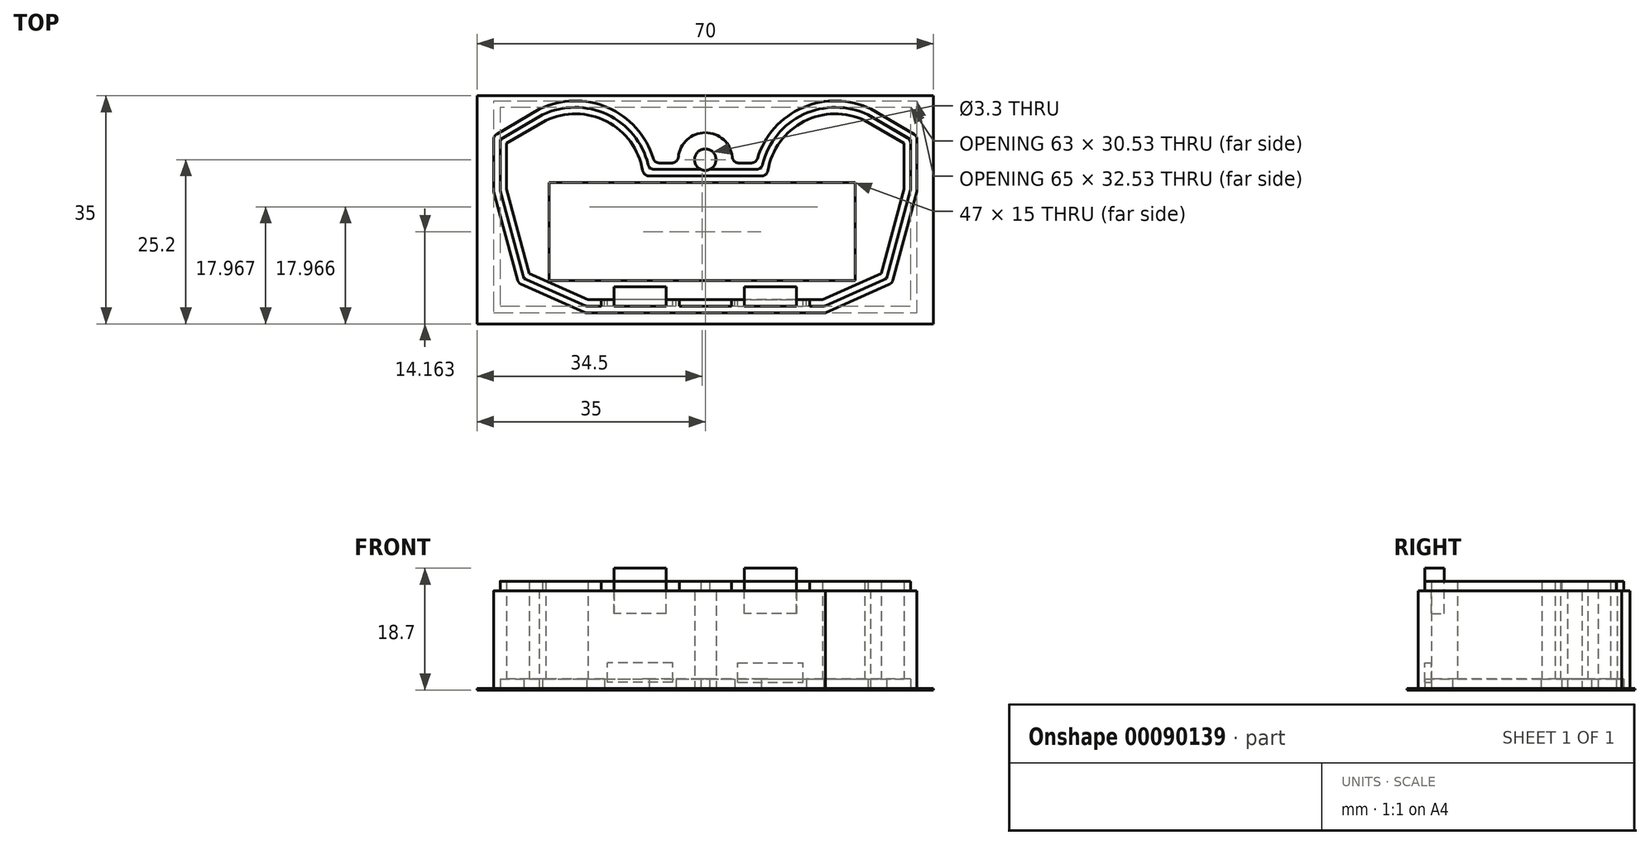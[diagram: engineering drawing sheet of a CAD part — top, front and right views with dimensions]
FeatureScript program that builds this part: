
annotation { "Feature Type Name" : "Feature", "Feature Type Description" : "" }
export const myFeature = defineFeature(function(context is Context, id is Id, definition is map)
    precondition{}
    {
        {
            var Q0;
            Q0=qCreatedBy(makeId("Top.planeOp"),FACE);
            var sketch = newSketch(context, id + "F0", { "sketchPlane" : qUnion([Q0])});
            skLineSegment(sketch, "E0", {"start": v(-31.6, 0) * mm, "end": v(0, 0) * mm, "construction": true});
            skLineSegment(sketch, "E1", {"start": v(-18, 0) * mm, "end": v(0, 0) * mm});
            skLineSegment(sketch, "E2", {"start": v(-27, 4) * mm, "end": v(0, 4) * mm, "construction": true});
            skLineSegment(sketch, "E3", {"start": v(-18, 0) * mm, "end": v(-27, 4) * mm});
            skLineSegment(sketch, "E4", {"start": v(-30.5, 17) * mm, "end": v(0, 17) * mm, "construction": true});
            skLineSegment(sketch, "E5", {"start": v(-30.5, 17) * mm, "end": v(-30.5, 24) * mm});
            skLineSegment(sketch, "E6", {"start": v(-30.5, 17) * mm, "end": v(-27, 4) * mm});
            skArc(sketch, "E7", {"start": v(0, 23.15) * mm, "mid": v(-1.65, 21.5) * mm, "end": v(0, 19.85) * mm});
            skLineSegment(sketch, "E8", {"start": v(0, 0) * mm, "end": v(0, 42.85) * mm, "construction": true});
            skLineSegment(sketch, "E9", {"start": v(-30.5, 24) * mm, "end": v(-24.5, 27.5) * mm});
            skLineSegment(sketch, "E10", {"start": v(0, 19) * mm, "end": v(-9.5, 19) * mm});
            skArc(sketch, "E11", {"start": v(-9.5, 19) * mm, "mid": v(-14.78, 27.17) * mm, "end": v(-24.5, 27.5) * mm});
            skLineSegment(sketch, "E12.0", {"start": v(-18.21, -1) * mm, "end": v(0, -1) * mm});
            skLineSegment(sketch, "E12.1", {"start": v(-18.21, -1) * mm, "end": v(-27.84, 3.28) * mm});
            skLineSegment(sketch, "E12.2", {"start": v(-31.5, 16.87) * mm, "end": v(-27.84, 3.28) * mm});
            skLineSegment(sketch, "E12.3", {"start": v(-0.69, 20) * mm, "end": v(-8.62, 20) * mm});
            skArc(sketch, "E12.4", {"start": v(-8.62, 20) * mm, "mid": v(-14.7, 28.27) * mm, "end": v(-24.97, 28.38) * mm});
            skLineSegment(sketch, "E12.5", {"start": v(-31.5, 24.57) * mm, "end": v(-24.97, 28.38) * mm});
            skLineSegment(sketch, "E12.6", {"start": v(-31.5, 16.87) * mm, "end": v(-31.5, 24.57) * mm});
            skLineSegment(sketch, "E13.MirrorCS", {"start": v(30.5, 24) * mm, "end": v(24.5, 27.5) * mm});
            skLineSegment(sketch, "E14.MirrorCS", {"start": v(18, 0) * mm, "end": v(0, 0) * mm});
            skLineSegment(sketch, "E15.MirrorCS", {"start": v(31.5, 16.87) * mm, "end": v(27.84, 3.28) * mm});
            skArc(sketch, "E16.MirrorCS", {"start": v(0, 23.15) * mm, "mid": v(1.65, 21.5) * mm, "end": v(0, 19.85) * mm});
            skLineSegment(sketch, "E17.MirrorCS", {"start": v(18, 0) * mm, "end": v(27, 4) * mm});
            skLineSegment(sketch, "E18.MirrorCS", {"start": v(30.5, 17) * mm, "end": v(27, 4) * mm});
            skLineSegment(sketch, "E19.MirrorCS", {"start": v(31.5, 24.57) * mm, "end": v(24.97, 28.38) * mm});
            skLineSegment(sketch, "E20.MirrorCS", {"start": v(27, 4) * mm, "end": v(0, 4) * mm, "construction": true});
            skArc(sketch, "E21.MirrorCS", {"start": v(9.5, 19) * mm, "mid": v(14.78, 27.17) * mm, "end": v(24.5, 27.5) * mm});
            skLineSegment(sketch, "E22.MirrorCS", {"start": v(31.5, 16.87) * mm, "end": v(31.5, 24.57) * mm});
            skLineSegment(sketch, "E23.MirrorCS", {"start": v(31.6, 0) * mm, "end": v(0, 0) * mm, "construction": true});
            skLineSegment(sketch, "E24.MirrorCS", {"start": v(18.21, -1) * mm, "end": v(0, -1) * mm});
            skLineSegment(sketch, "E25.MirrorCS", {"start": v(0.69, 20) * mm, "end": v(8.62, 20) * mm});
            skLineSegment(sketch, "E26.MirrorCS", {"start": v(18.21, -1) * mm, "end": v(27.84, 3.28) * mm});
            skLineSegment(sketch, "E27.MirrorCS", {"start": v(0, 19) * mm, "end": v(9.5, 19) * mm});
            skLineSegment(sketch, "E28.MirrorCS", {"start": v(30.5, 17) * mm, "end": v(30.5, 24) * mm});
            skArc(sketch, "E29.MirrorCS", {"start": v(8.62, 20) * mm, "mid": v(14.7, 28.27) * mm, "end": v(24.97, 28.38) * mm});
            skLineSegment(sketch, "E30.0", {"start": v(-18.42, -2) * mm, "end": v(0, -2) * mm});
            skLineSegment(sketch, "E30.1", {"start": v(18.42, -2) * mm, "end": v(0, -2) * mm});
            skLineSegment(sketch, "E30.2", {"start": v(18.42, -2) * mm, "end": v(28.68, 2.56) * mm});
            skArc(sketch, "E30.3", {"start": v(-7.81, 21) * mm, "mid": v(-14.65, 29.35) * mm, "end": v(-25.44, 29.27) * mm});
            skLineSegment(sketch, "E30.4", {"start": v(-32.5, 25.15) * mm, "end": v(-25.44, 29.27) * mm});
            skLineSegment(sketch, "E30.5", {"start": v(-32.5, 16.74) * mm, "end": v(-32.5, 25.15) * mm});
            skLineSegment(sketch, "E30.6", {"start": v(-32.5, 16.74) * mm, "end": v(-28.68, 2.56) * mm});
            skLineSegment(sketch, "E30.7", {"start": v(-4.12, 21) * mm, "end": v(-7.81, 21) * mm});
            skLineSegment(sketch, "E30.8", {"start": v(4.12, 21) * mm, "end": v(7.81, 21) * mm});
            skArc(sketch, "E30.9", {"start": v(7.81, 21) * mm, "mid": v(14.65, 29.35) * mm, "end": v(25.44, 29.27) * mm});
            skLineSegment(sketch, "E30.10", {"start": v(-18.42, -2) * mm, "end": v(-28.68, 2.56) * mm});
            skLineSegment(sketch, "E30.11", {"start": v(32.5, 25.15) * mm, "end": v(25.44, 29.27) * mm});
            skLineSegment(sketch, "E30.12", {"start": v(32.5, 16.74) * mm, "end": v(32.5, 25.15) * mm});
            skLineSegment(sketch, "E30.13", {"start": v(32.5, 16.74) * mm, "end": v(28.68, 2.56) * mm});
            skArc(sketch, "E31.0", {"start": v(0, 25.65) * mm, "mid": v(-3.1, 24.25) * mm, "end": v(-4.12, 21) * mm});
            skArc(sketch, "E31.1", {"start": v(0, 25.65) * mm, "mid": v(3.1, 24.25) * mm, "end": v(4.12, 21) * mm});
            skPoint(sketch, "E32.orphan", {"position": v(0, 20) * mm});
            skSolve(sketch);
        }
        {
            var Q0;
            Q0=makeQuery(id+"F0.imprint","IMPRINT",FACE,{"disambiguationData":[TD([[makeQuery(id+"F0.imprint","IMPRINT",EDGE,{"derivedFrom":sQuery(id+"F0.wireOp",EDGE,"E1")}),-1.0]])]});
            extrude(context, id + "F1", {"entities" : qUnion([Q0]), "depth" : 1.5 * mm, "offsetDistance" : 25 * mm});
        }
        {
            var Q0;
            Q0 = qSketchRegion(id + "F0", true);
            var Q1;
            Q1=makeQuery(id+"F1.opExtrude","CAP_FACE",FACE,{"disambiguationData":[OSD([sQuery(id+"F0.wireOp",EDGE,"E1"),sQuery(id+"F0.wireOp",EDGE,"E3"),sQuery(id+"F0.wireOp",EDGE,"E5"),sQuery(id+"F0.wireOp",EDGE,"E6"),sQuery(id+"F0.wireOp",EDGE,"E7"),sQuery(id+"F0.wireOp",EDGE,"E9"),sQuery(id+"F0.wireOp",EDGE,"E10"),sQuery(id+"F0.wireOp",EDGE,"E11"),sQuery(id+"F0.wireOp",EDGE,"E12.0"),sQuery(id+"F0.wireOp",EDGE,"E12.1"),sQuery(id+"F0.wireOp",EDGE,"E12.2"),sQuery(id+"F0.wireOp",EDGE,"E12.3"),sQuery(id+"F0.wireOp",EDGE,"E12.4"),sQuery(id+"F0.wireOp",EDGE,"E12.5"),sQuery(id+"F0.wireOp",EDGE,"E12.6"),sQuery(id+"F0.wireOp",EDGE,"E13.MirrorCS"),sQuery(id+"F0.wireOp",EDGE,"E14.MirrorCS"),sQuery(id+"F0.wireOp",EDGE,"E15.MirrorCS"),sQuery(id+"F0.wireOp",EDGE,"E16.MirrorCS"),sQuery(id+"F0.wireOp",EDGE,"E17.MirrorCS"),sQuery(id+"F0.wireOp",EDGE,"E18.MirrorCS"),sQuery(id+"F0.wireOp",EDGE,"E19.MirrorCS"),sQuery(id+"F0.wireOp",EDGE,"E21.MirrorCS"),sQuery(id+"F0.wireOp",EDGE,"E22.MirrorCS"),sQuery(id+"F0.wireOp",EDGE,"E24.MirrorCS"),sQuery(id+"F0.wireOp",EDGE,"E25.MirrorCS"),sQuery(id+"F0.wireOp",EDGE,"E26.MirrorCS"),sQuery(id+"F0.wireOp",EDGE,"E27.MirrorCS"),sQuery(id+"F0.wireOp",EDGE,"E28.MirrorCS"),sQuery(id+"F0.wireOp",EDGE,"E29.MirrorCS")])],"isStart":true});
            extrude(context, id + "F2", {"entities" : qUnion([Q0, Q1]), "operationType" : NewBodyOperationType.ADD, "surfaceOperationType" : NewSurfaceOperationType.ADD, "oppositeDirection" : true, "depth" : 15 * mm, "offsetDistance" : 25 * mm});
        }
        {
            var Q0;
            Q0=makeQuery(id+"F2.opExtrude","SWEPT_EDGE",EDGE,{"disambiguationData":[OSD([sQuery(id+"F0.wireOp",EDGE,"E30.8"),sQuery(id+"F0.wireOp",EDGE,"E30.9")])]});
            var Q1;
            Q1=makeQuery(id+"F2.opExtrude","SWEPT_EDGE",EDGE,{"disambiguationData":[OSD([sQuery(id+"F0.wireOp",EDGE,"E30.3"),sQuery(id+"F0.wireOp",EDGE,"E30.7")])]});
            var Q2;
            Q2=makeQuery(id+"F2.opExtrude","SWEPT_EDGE",EDGE,{"disambiguationData":[OSD([sQuery(id+"F0.wireOp",EDGE,"E30.7"),sQuery(id+"F0.wireOp",EDGE,"E31.0")])]});
            var Q3;
            Q3=makeQuery(id+"F2.opExtrude","SWEPT_EDGE",EDGE,{"disambiguationData":[OSD([sQuery(id+"F0.wireOp",EDGE,"E30.8"),sQuery(id+"F0.wireOp",EDGE,"E31.1")])]});
            var Q4;
            Q4=makeQuery(id+"F2.opExtrude","SWEPT_EDGE",EDGE,{"disambiguationData":[OSD([sQuery(id+"F0.wireOp",EDGE,"E30.11"),sQuery(id+"F0.wireOp",EDGE,"E30.12")])]});
            var Q5;
            Q5=makeQuery(id+"F2.opExtrude","SWEPT_EDGE",EDGE,{"disambiguationData":[OSD([sQuery(id+"F0.wireOp",EDGE,"E30.12"),sQuery(id+"F0.wireOp",EDGE,"E30.13")])]});
            var Q6;
            Q6=makeQuery(id+"F2.opExtrude","SWEPT_EDGE",EDGE,{"disambiguationData":[OSD([sQuery(id+"F0.wireOp",EDGE,"E30.2"),sQuery(id+"F0.wireOp",EDGE,"E30.13")])]});
            var Q7;
            Q7=makeQuery(id+"F2.opExtrude","SWEPT_EDGE",EDGE,{"disambiguationData":[OSD([sQuery(id+"F0.wireOp",EDGE,"E30.0"),sQuery(id+"F0.wireOp",EDGE,"E30.10")])]});
            var Q8;
            Q8=makeQuery(id+"F2.opExtrude","SWEPT_EDGE",EDGE,{"disambiguationData":[OSD([sQuery(id+"F0.wireOp",EDGE,"E30.6"),sQuery(id+"F0.wireOp",EDGE,"E30.10")])]});
            var Q9;
            Q9=makeQuery(id+"F2.opExtrude","SWEPT_EDGE",EDGE,{"disambiguationData":[OSD([sQuery(id+"F0.wireOp",EDGE,"E30.5"),sQuery(id+"F0.wireOp",EDGE,"E30.6")])]});
            var Q10;
            Q10=makeQuery(id+"F2.opExtrude","SWEPT_EDGE",EDGE,{"disambiguationData":[OSD([sQuery(id+"F0.wireOp",EDGE,"E30.4"),sQuery(id+"F0.wireOp",EDGE,"E30.5")])]});
            var Q11;
            Q11=makeQuery(id+"F1.opExtrude","SWEPT_EDGE",EDGE,{"disambiguationData":[OSD([sQuery(id+"F0.wireOp",EDGE,"E19.MirrorCS"),sQuery(id+"F0.wireOp",EDGE,"E22.MirrorCS")])]});
            var Q12;
            Q12=makeQuery(id+"F1.opExtrude","SWEPT_EDGE",EDGE,{"disambiguationData":[OSD([sQuery(id+"F0.wireOp",EDGE,"E15.MirrorCS"),sQuery(id+"F0.wireOp",EDGE,"E22.MirrorCS")])]});
            var Q13;
            Q13=makeQuery(id+"F1.opExtrude","SWEPT_EDGE",EDGE,{"disambiguationData":[OSD([sQuery(id+"F0.wireOp",EDGE,"E15.MirrorCS"),sQuery(id+"F0.wireOp",EDGE,"E26.MirrorCS")])]});
            var Q14;
            Q14=makeQuery(id+"F1.opExtrude","SWEPT_EDGE",EDGE,{"disambiguationData":[OSD([sQuery(id+"F0.wireOp",EDGE,"E24.MirrorCS"),sQuery(id+"F0.wireOp",EDGE,"E26.MirrorCS")])]});
            var Q15;
            Q15=makeQuery(id+"F1.opExtrude","SWEPT_EDGE",EDGE,{"disambiguationData":[OSD([sQuery(id+"F0.wireOp",EDGE,"E12.0"),sQuery(id+"F0.wireOp",EDGE,"E12.1")])]});
            var Q16;
            Q16=makeQuery(id+"F1.opExtrude","SWEPT_EDGE",EDGE,{"disambiguationData":[OSD([sQuery(id+"F0.wireOp",EDGE,"E12.1"),sQuery(id+"F0.wireOp",EDGE,"E12.2")])]});
            var Q17;
            Q17=makeQuery(id+"F1.opExtrude","SWEPT_EDGE",EDGE,{"disambiguationData":[OSD([sQuery(id+"F0.wireOp",EDGE,"E12.2"),sQuery(id+"F0.wireOp",EDGE,"E12.6")])]});
            var Q18;
            Q18=makeQuery(id+"F1.opExtrude","SWEPT_EDGE",EDGE,{"disambiguationData":[OSD([sQuery(id+"F0.wireOp",EDGE,"E12.5"),sQuery(id+"F0.wireOp",EDGE,"E12.6")])]});
            var Q19;
            Q19=makeQuery(id+"F1.opExtrude","SWEPT_EDGE",EDGE,{"disambiguationData":[OSD([sQuery(id+"F0.wireOp",EDGE,"E12.3"),sQuery(id+"F0.wireOp",EDGE,"E12.4")])]});
            var Q20;
            Q20=makeQuery(id+"F1.opExtrude","SWEPT_EDGE",EDGE,{"disambiguationData":[OSD([sQuery(id+"F0.wireOp",EDGE,"E25.MirrorCS"),sQuery(id+"F0.wireOp",EDGE,"E29.MirrorCS")])]});
            var Q21;
            {var subQ0=sQuery(id+"F0.wireOp",EDGE,"E27.MirrorCS");var subQ1=sQuery(id+"F0.wireOp",EDGE,"E21.MirrorCS");Q21=makeQuery(id+"F2.boolean.opBoolean","MERGE",EDGE,{"derivedFrom":[makeQuery(id+"F1.opExtrude","SWEPT_EDGE",EDGE,{"disambiguationData":[OSD([subQ1,subQ0])]}),makeQuery(id+"F2.opExtrude","SWEPT_EDGE",EDGE,{"disambiguationData":[OSD([subQ1,subQ0])]})]});}
            var Q22;
            {var subQ0=sQuery(id+"F0.wireOp",EDGE,"E11");var subQ1=sQuery(id+"F0.wireOp",EDGE,"E10");Q22=makeQuery(id+"F2.boolean.opBoolean","MERGE",EDGE,{"derivedFrom":[makeQuery(id+"F1.opExtrude","SWEPT_EDGE",EDGE,{"disambiguationData":[OSD([subQ1,subQ0])]}),makeQuery(id+"F2.opExtrude","SWEPT_EDGE",EDGE,{"disambiguationData":[OSD([subQ1,subQ0])]})]});}
            fillet(context, id + "F3", {"entities" : qUnion([Q0, Q1, Q2, Q3, Q4, Q5, Q6, Q7, Q8, Q9, Q10, Q11, Q12, Q13, Q14, Q15, Q16, Q17, Q18, Q19, Q20, Q21, Q22]), "tangentPropagation" : true, "radius" : 1 * mm, "defaultsChanged" : false, "vertexSettings" : [], "allowEdgeOverflow" : false});
        }
        {
            var Q0;
            {var subQ0=sQuery(id+"F0.wireOp",EDGE,"E29.MirrorCS");var subQ1=sQuery(id+"F0.wireOp",EDGE,"E26.MirrorCS");var subQ2=sQuery(id+"F0.wireOp",EDGE,"E25.MirrorCS");var subQ3=sQuery(id+"F0.wireOp",EDGE,"E24.MirrorCS");var subQ4=sQuery(id+"F0.wireOp",EDGE,"E22.MirrorCS");var subQ5=sQuery(id+"F0.wireOp",EDGE,"E19.MirrorCS");var subQ6=sQuery(id+"F0.wireOp",EDGE,"E16.MirrorCS");var subQ7=sQuery(id+"F0.wireOp",EDGE,"E15.MirrorCS");var subQ8=sQuery(id+"F0.wireOp",EDGE,"E12.6");var subQ9=sQuery(id+"F0.wireOp",EDGE,"E12.5");var subQ10=sQuery(id+"F0.wireOp",EDGE,"E12.4");var subQ11=sQuery(id+"F0.wireOp",EDGE,"E12.3");var subQ12=sQuery(id+"F0.wireOp",EDGE,"E12.2");var subQ13=sQuery(id+"F0.wireOp",EDGE,"E12.1");var subQ14=sQuery(id+"F0.wireOp",EDGE,"E12.0");var subQ15=sQuery(id+"F0.wireOp",EDGE,"E7");Q0=makeQuery(id+"F2.boolean.opBoolean","MERGE",FACE,{"derivedFrom":[makeQuery(id+"F2.opExtrude","CAP_FACE",FACE,{"disambiguationData":[OSD([subQ15,subQ14,subQ13,subQ12,subQ11,subQ10,subQ9,subQ8,subQ7,subQ6,subQ5,subQ4,subQ3,subQ2,subQ1,subQ0,sQuery(id+"F0.wireOp",EDGE,"E30.0"),sQuery(id+"F0.wireOp",EDGE,"E30.1"),sQuery(id+"F0.wireOp",EDGE,"E30.2"),sQuery(id+"F0.wireOp",EDGE,"E30.3"),sQuery(id+"F0.wireOp",EDGE,"E30.4"),sQuery(id+"F0.wireOp",EDGE,"E30.5"),sQuery(id+"F0.wireOp",EDGE,"E30.6"),sQuery(id+"F0.wireOp",EDGE,"E30.7"),sQuery(id+"F0.wireOp",EDGE,"E30.8"),sQuery(id+"F0.wireOp",EDGE,"E30.9"),sQuery(id+"F0.wireOp",EDGE,"E30.10"),sQuery(id+"F0.wireOp",EDGE,"E30.11"),sQuery(id+"F0.wireOp",EDGE,"E30.12"),sQuery(id+"F0.wireOp",EDGE,"E30.13"),sQuery(id+"F0.wireOp",EDGE,"E31.0"),sQuery(id+"F0.wireOp",EDGE,"E31.1")])],"isStart":false}),makeQuery(id+"F2.opExtrude","CAP_FACE",FACE,{"disambiguationData":[OSD([sQuery(id+"F0.wireOp",EDGE,"E1"),sQuery(id+"F0.wireOp",EDGE,"E3"),sQuery(id+"F0.wireOp",EDGE,"E5"),sQuery(id+"F0.wireOp",EDGE,"E6"),subQ15,sQuery(id+"F0.wireOp",EDGE,"E9"),sQuery(id+"F0.wireOp",EDGE,"E10"),sQuery(id+"F0.wireOp",EDGE,"E11"),subQ14,subQ13,subQ12,subQ11,subQ10,subQ9,subQ8,sQuery(id+"F0.wireOp",EDGE,"E13.MirrorCS"),sQuery(id+"F0.wireOp",EDGE,"E14.MirrorCS"),subQ7,subQ6,sQuery(id+"F0.wireOp",EDGE,"E17.MirrorCS"),sQuery(id+"F0.wireOp",EDGE,"E18.MirrorCS"),subQ5,sQuery(id+"F0.wireOp",EDGE,"E21.MirrorCS"),subQ4,subQ3,subQ2,subQ1,sQuery(id+"F0.wireOp",EDGE,"E27.MirrorCS"),sQuery(id+"F0.wireOp",EDGE,"E28.MirrorCS"),subQ0])],"isStart":false})]});}
            var sketch = newSketch(context, id + "F4", { "sketchPlane" : qUnion([Q0])});
            skLineSegment(sketch, "E33.0", {"start": v(18, 0) * mm, "end": v(-18, 0) * mm});
            skLineSegment(sketch, "E34.0", {"start": v(-18, 0) * mm, "end": v(-27, -4) * mm});
            skLineSegment(sketch, "E35.0", {"start": v(-30.5, -17) * mm, "end": v(-27, -4) * mm});
            skLineSegment(sketch, "E36.0", {"start": v(-30.5, -17) * mm, "end": v(-30.5, -24) * mm});
            skLineSegment(sketch, "E37.0", {"start": v(-30.5, -24) * mm, "end": v(-24.5, -27.5) * mm});
            skArc(sketch, "E38.0", {"start": v(-9.61, -19.83) * mm, "mid": v(-15.15, -27.37) * mm, "end": v(-24.5, -27.5) * mm});
            skPoint(sketch, "E39.0", {"position": v(-9.27, -19.23) * mm});
            skPoint(sketch, "E40.0", {"position": v(9.27, -19.23) * mm});
            skArc(sketch, "E41.0", {"start": v(9.61, -19.83) * mm, "mid": v(15.15, -27.37) * mm, "end": v(24.5, -27.5) * mm});
            skPoint(sketch, "E42.0", {"position": v(27.5, -25.75) * mm});
            skLineSegment(sketch, "E43.0", {"start": v(30.5, -17) * mm, "end": v(30.5, -24) * mm});
            skLineSegment(sketch, "E44.0", {"start": v(30.5, -17) * mm, "end": v(27, -4) * mm});
            skLineSegment(sketch, "E45.0", {"start": v(18, 0) * mm, "end": v(27, -4) * mm});
            skLineSegment(sketch, "E46.0", {"start": v(18.21, 1) * mm, "end": v(27.84, -3.28) * mm});
            skLineSegment(sketch, "E46.1", {"start": v(-31.5, -24.57) * mm, "end": v(-24.97, -28.38) * mm});
            skLineSegment(sketch, "E46.2", {"start": v(-31.5, -16.87) * mm, "end": v(-31.5, -24.57) * mm});
            skLineSegment(sketch, "E46.3", {"start": v(-31.5, -16.87) * mm, "end": v(-27.84, -3.28) * mm});
            skLineSegment(sketch, "E46.4", {"start": v(-18.21, 1) * mm, "end": v(-27.84, -3.28) * mm});
            skArc(sketch, "E46.5", {"start": v(-8.62, -20) * mm, "mid": v(-14.7, -28.27) * mm, "end": v(-24.97, -28.38) * mm});
            skLineSegment(sketch, "E46.6", {"start": v(18.21, 1) * mm, "end": v(-18.21, 1) * mm});
            skLineSegment(sketch, "E46.7", {"start": v(8.62, -20) * mm, "end": v(-8.62, -20) * mm});
            skArc(sketch, "E46.8", {"start": v(8.62, -20) * mm, "mid": v(14.7, -28.27) * mm, "end": v(24.97, -28.38) * mm});
            skLineSegment(sketch, "E46.9", {"start": v(31.5, -24.57) * mm, "end": v(24.97, -28.38) * mm});
            skLineSegment(sketch, "E46.10", {"start": v(31.5, -16.87) * mm, "end": v(31.5, -24.57) * mm});
            skLineSegment(sketch, "E46.11", {"start": v(31.5, -16.87) * mm, "end": v(27.84, -3.28) * mm});
            skSolve(sketch);
        }
        {
            var Q0;
            Q0 = qSketchRegion(id + "F4", true);
            extrude(context, id + "F5", {"entities" : qUnion([Q0]), "operationType" : NewBodyOperationType.REMOVE, "oppositeDirection" : true, "depth" : 1.5 * mm, "offsetDistance" : 25 * mm});
        }
        {
            var Q0;
            {var subQ0=sQuery(id+"F0.wireOp",EDGE,"E14.MirrorCS");var subQ1=sQuery(id+"F0.wireOp",EDGE,"E1");Q0=makeQuery(id+"F2.boolean.opBoolean","MERGE",FACE,{"derivedFrom":[makeQuery(id+"F1.opExtrude","SWEPT_FACE",FACE,{"disambiguationData":[OSD([subQ1,subQ0])]}),makeQuery(id+"F2.opExtrude","SWEPT_FACE",FACE,{"disambiguationData":[OSD([subQ1,subQ0])]})]});}
            var sketch = newSketch(context, id + "F6", { "sketchPlane" : qUnion([Q0])});
            skLineSegment(sketch, "E47", {"start": v(0, -13.5) * mm, "end": v(4.5, -13.5) * mm, "construction": true});
            skLineSegment(sketch, "E48.bottom", {"start": v(4.5, -13.5) * mm, "end": v(15.5, -13.5) * mm});
            skLineSegment(sketch, "E48.top", {"start": v(4.5, -15) * mm, "end": v(15.5, -15) * mm});
            skLineSegment(sketch, "E48.left", {"start": v(4.5, -13.5) * mm, "end": v(4.5, -15) * mm});
            skLineSegment(sketch, "E48.right", {"start": v(15.5, -13.5) * mm, "end": v(15.5, -15) * mm});
            skLineSegment(sketch, "E49", {"start": v(0, -13.5) * mm, "end": v(0, -15.77) * mm, "construction": true});
            skLineSegment(sketch, "E50.MirrorCS", {"start": v(-4.5, -15) * mm, "end": v(-15.5, -15) * mm});
            skLineSegment(sketch, "E51.MirrorCS", {"start": v(-4.5, -13.5) * mm, "end": v(-4.5, -15) * mm});
            skLineSegment(sketch, "E52.MirrorCS", {"start": v(-15.5, -13.5) * mm, "end": v(-15.5, -15) * mm});
            skLineSegment(sketch, "E53.MirrorCS", {"start": v(-4.5, -13.5) * mm, "end": v(-15.5, -13.5) * mm});
            skSolve(sketch);
        }
        {
            var Q0;
            Q0 = qSketchRegion(id + "F6", true);
            extrude(context, id + "F7", {"entities" : qUnion([Q0]), "operationType" : NewBodyOperationType.ADD, "endBound" : BoundingType.UP_TO_NEXT, "oppositeDirection" : true, "depth" : 25 * mm, "offsetDistance" : 25 * mm});
        }
        {
            var Q0;
            {var subQ0=sQuery(id+"F0.wireOp",EDGE,"E14.MirrorCS");var subQ1=sQuery(id+"F0.wireOp",EDGE,"E1");Q0=makeQuery(id+"F2.boolean.opBoolean","MERGE",FACE,{"derivedFrom":[makeQuery(id+"F1.opExtrude","SWEPT_FACE",FACE,{"disambiguationData":[OSD([subQ1,subQ0])]}),makeQuery(id+"F2.opExtrude","SWEPT_FACE",FACE,{"disambiguationData":[OSD([subQ1,subQ0])]})]});}
            var sketch = newSketch(context, id + "F8", { "sketchPlane" : qUnion([Q0])});
            skLineSegment(sketch, "E54.bottom", {"start": v(-5, -14) * mm, "end": v(-15, -14) * mm});
            skLineSegment(sketch, "E54.top", {"start": v(-5, -11) * mm, "end": v(-15, -11) * mm});
            skLineSegment(sketch, "E54.left", {"start": v(-5, -14) * mm, "end": v(-5, -11) * mm});
            skLineSegment(sketch, "E54.right", {"start": v(-15, -14) * mm, "end": v(-15, -11) * mm});
            skLineSegment(sketch, "E55", {"start": v(0, 0) * mm, "end": v(0, -29.26) * mm, "construction": true});
            skLineSegment(sketch, "E56.MirrorCS", {"start": v(5, -11) * mm, "end": v(15, -11) * mm});
            skLineSegment(sketch, "E57.MirrorCS", {"start": v(5, -14) * mm, "end": v(5, -11) * mm});
            skLineSegment(sketch, "E58.MirrorCS", {"start": v(5, -14) * mm, "end": v(15, -14) * mm});
            skLineSegment(sketch, "E59.MirrorCS", {"start": v(15, -14) * mm, "end": v(15, -11) * mm});
            skSolve(sketch);
        }
        {
            var Q0;
            Q0 = qSketchRegion(id + "F8", true);
            extrude(context, id + "F9", {"entities" : qUnion([Q0]), "operationType" : NewBodyOperationType.REMOVE, "oppositeDirection" : true, "depth" : 1 * mm, "offsetDistance" : 25 * mm});
        }
        {
            var Q0;
            Q0=makeQuery(id+"F1.opExtrude","CAP_FACE",FACE,{"disambiguationData":[OSD([sQuery(id+"F0.wireOp",EDGE,"E1"),sQuery(id+"F0.wireOp",EDGE,"E3"),sQuery(id+"F0.wireOp",EDGE,"E5"),sQuery(id+"F0.wireOp",EDGE,"E6"),sQuery(id+"F0.wireOp",EDGE,"E7"),sQuery(id+"F0.wireOp",EDGE,"E9"),sQuery(id+"F0.wireOp",EDGE,"E10"),sQuery(id+"F0.wireOp",EDGE,"E11"),sQuery(id+"F0.wireOp",EDGE,"E12.0"),sQuery(id+"F0.wireOp",EDGE,"E12.1"),sQuery(id+"F0.wireOp",EDGE,"E12.2"),sQuery(id+"F0.wireOp",EDGE,"E12.3"),sQuery(id+"F0.wireOp",EDGE,"E12.4"),sQuery(id+"F0.wireOp",EDGE,"E12.5"),sQuery(id+"F0.wireOp",EDGE,"E12.6"),sQuery(id+"F0.wireOp",EDGE,"E13.MirrorCS"),sQuery(id+"F0.wireOp",EDGE,"E14.MirrorCS"),sQuery(id+"F0.wireOp",EDGE,"E15.MirrorCS"),sQuery(id+"F0.wireOp",EDGE,"E16.MirrorCS"),sQuery(id+"F0.wireOp",EDGE,"E17.MirrorCS"),sQuery(id+"F0.wireOp",EDGE,"E18.MirrorCS"),sQuery(id+"F0.wireOp",EDGE,"E19.MirrorCS"),sQuery(id+"F0.wireOp",EDGE,"E21.MirrorCS"),sQuery(id+"F0.wireOp",EDGE,"E22.MirrorCS"),sQuery(id+"F0.wireOp",EDGE,"E24.MirrorCS"),sQuery(id+"F0.wireOp",EDGE,"E25.MirrorCS"),sQuery(id+"F0.wireOp",EDGE,"E26.MirrorCS"),sQuery(id+"F0.wireOp",EDGE,"E27.MirrorCS"),sQuery(id+"F0.wireOp",EDGE,"E28.MirrorCS"),sQuery(id+"F0.wireOp",EDGE,"E29.MirrorCS")])],"isStart":false});
            var sketch = newSketch(context, id + "F10", { "sketchPlane" : qUnion([Q0])});
            skLineSegment(sketch, "E60", {"start": v(0, 0) * mm, "end": v(6, 0) * mm, "construction": true});
            skLineSegment(sketch, "E61", {"start": v(6, 0) * mm, "end": v(6, 2) * mm});
            skLineSegment(sketch, "E62", {"start": v(6, 2) * mm, "end": v(14, 2) * mm});
            skLineSegment(sketch, "E63", {"start": v(14, 2) * mm, "end": v(14, -1) * mm});
            skLineSegment(sketch, "E64", {"start": v(14, -1) * mm, "end": v(6, -1) * mm});
            skLineSegment(sketch, "E65", {"start": v(6, -1) * mm, "end": v(6, 0) * mm});
            skLineSegment(sketch, "E66", {"start": v(0, 0) * mm, "end": v(0, -5.28) * mm, "construction": true});
            skPoint(sketch, "E66.endSnap0", {"position": v(0, -1) * mm});
            skLineSegment(sketch, "E67.MirrorCS", {"start": v(-6, 2) * mm, "end": v(-14, 2) * mm});
            skLineSegment(sketch, "E68.MirrorCS", {"start": v(-14, 2) * mm, "end": v(-14, -1) * mm});
            skLineSegment(sketch, "E69.MirrorCS", {"start": v(-14, -1) * mm, "end": v(-6, -1) * mm});
            skLineSegment(sketch, "E70.MirrorCS", {"start": v(-6, -1) * mm, "end": v(-6, 0) * mm});
            skLineSegment(sketch, "E71.MirrorCS", {"start": v(-6, 0) * mm, "end": v(-6, 2) * mm});
            skSolve(sketch);
        }
        {
            var Q0;
            {var subQ0=sQuery(id+"F10.wireOp",EDGE,"E64");Q0=makeQuery(id+"F10.imprint","IMPRINT",FACE,{"disambiguationData":[TD([[makeQuery(id+"F10.imprint","IMPRINT",EDGE,{"derivedFrom":subQ0}),1.0]])]});}
            var Q1;
            {var subQ0=sQuery(id+"F10.wireOp",EDGE,"E69.MirrorCS");Q1=makeQuery(id+"F10.imprint","IMPRINT",FACE,{"disambiguationData":[TD([[makeQuery(id+"F10.imprint","IMPRINT",EDGE,{"derivedFrom":subQ0}),1.0]])]});}
            var Q2;
            {var subQ0=sQuery(id+"F10.wireOp",EDGE,"E67.MirrorCS");Q2=makeQuery(id+"F10.imprint","IMPRINT",FACE,{"disambiguationData":[TD([[makeQuery(id+"F10.imprint","IMPRINT",EDGE,{"derivedFrom":subQ0}),1.0]])]});}
            var Q3;
            {var subQ0=sQuery(id+"F10.wireOp",EDGE,"E61");Q3=makeQuery(id+"F10.imprint","IMPRINT",FACE,{"disambiguationData":[TD([[makeQuery(id+"F10.imprint","IMPRINT",EDGE,{"derivedFrom":subQ0}),-1.0]])]});}
            extrude(context, id + "F11", {"entities" : qUnion([Q0, Q1, Q2, Q3]), "operationType" : NewBodyOperationType.ADD, "oppositeDirection" : true, "depth" : 5 * mm, "offsetDistance" : 25 * mm, "hasSecondDirection" : true, "secondDirectionOppositeDirection" : false, "secondDirectionDepth" : 2 * mm});
        }
        {
            var Q0;
            Q0=makeQuery(id+"F11.boolean.opBoolean","MERGE",FACE,{"derivedFrom":[makeQuery(id+"F1.opExtrude","SWEPT_FACE",FACE,{"disambiguationData":[OSD([sQuery(id+"F0.wireOp",EDGE,"E12.0"),sQuery(id+"F0.wireOp",EDGE,"E24.MirrorCS")])]}),makeQuery(id+"F11.opExtrude","SWEPT_FACE",FACE,{"disambiguationData":[OSD([sQuery(id+"F10.wireOp",EDGE,"E64")])]}),makeQuery(id+"F11.opExtrude","SWEPT_FACE",FACE,{"disambiguationData":[OSD([sQuery(id+"F10.wireOp",EDGE,"E69.MirrorCS")])]})]});
            var sketch = newSketch(context, id + "F12", { "sketchPlane" : qUnion([Q0])});
            skLineSegment(sketch, "E72.bottom", {"start": v(-16, 1.5) * mm, "end": v(-4, 1.5) * mm});
            skLineSegment(sketch, "E72.top", {"start": v(-16, 0) * mm, "end": v(-4, 0) * mm});
            skLineSegment(sketch, "E72.left", {"start": v(-16, 1.5) * mm, "end": v(-16, 0) * mm});
            skLineSegment(sketch, "E72.right", {"start": v(-4, 1.5) * mm, "end": v(-4, 0) * mm});
            skLineSegment(sketch, "E73.MirrorCS", {"start": v(16, 1.5) * mm, "end": v(4, 1.5) * mm});
            skLineSegment(sketch, "E74.MirrorCS", {"start": v(4, 1.5) * mm, "end": v(4, 0) * mm});
            skLineSegment(sketch, "E75.MirrorCS", {"start": v(16, 1.5) * mm, "end": v(16, 0) * mm});
            skLineSegment(sketch, "E76.MirrorCS", {"start": v(16, 0) * mm, "end": v(4, 0) * mm});
            skSolve(sketch);
        }
        {
            var Q0;
            Q0 = qSketchRegion(id + "F12", true);
            extrude(context, id + "F13", {"entities" : qUnion([Q0]), "operationType" : NewBodyOperationType.REMOVE, "oppositeDirection" : true, "depth" : 1 * mm, "offsetDistance" : 25 * mm});
        }
        {
            var Q0;
            {var subQ0=sQuery(id+"F0.wireOp",EDGE,"E29.MirrorCS");var subQ1=sQuery(id+"F0.wireOp",EDGE,"E26.MirrorCS");var subQ2=sQuery(id+"F0.wireOp",EDGE,"E25.MirrorCS");var subQ3=sQuery(id+"F0.wireOp",EDGE,"E24.MirrorCS");var subQ4=sQuery(id+"F0.wireOp",EDGE,"E22.MirrorCS");var subQ5=sQuery(id+"F0.wireOp",EDGE,"E19.MirrorCS");var subQ6=sQuery(id+"F0.wireOp",EDGE,"E16.MirrorCS");var subQ7=sQuery(id+"F0.wireOp",EDGE,"E15.MirrorCS");var subQ8=sQuery(id+"F0.wireOp",EDGE,"E12.6");var subQ9=sQuery(id+"F0.wireOp",EDGE,"E12.5");var subQ10=sQuery(id+"F0.wireOp",EDGE,"E12.4");var subQ11=sQuery(id+"F0.wireOp",EDGE,"E12.3");var subQ12=sQuery(id+"F0.wireOp",EDGE,"E12.2");var subQ13=sQuery(id+"F0.wireOp",EDGE,"E12.1");var subQ14=sQuery(id+"F0.wireOp",EDGE,"E12.0");var subQ15=sQuery(id+"F0.wireOp",EDGE,"E7");Q0=makeQuery(id+"F7.boolean.opBoolean","MERGE",FACE,{"derivedFrom":[makeQuery(id+"F2.boolean.opBoolean","MERGE",FACE,{"derivedFrom":[makeQuery(id+"F2.opExtrude","CAP_FACE",FACE,{"disambiguationData":[OSD([subQ15,subQ14,subQ13,subQ12,subQ11,subQ10,subQ9,subQ8,subQ7,subQ6,subQ5,subQ4,subQ3,subQ2,subQ1,subQ0,sQuery(id+"F0.wireOp",EDGE,"E30.0"),sQuery(id+"F0.wireOp",EDGE,"E30.1"),sQuery(id+"F0.wireOp",EDGE,"E30.2"),sQuery(id+"F0.wireOp",EDGE,"E30.3"),sQuery(id+"F0.wireOp",EDGE,"E30.4"),sQuery(id+"F0.wireOp",EDGE,"E30.5"),sQuery(id+"F0.wireOp",EDGE,"E30.6"),sQuery(id+"F0.wireOp",EDGE,"E30.7"),sQuery(id+"F0.wireOp",EDGE,"E30.8"),sQuery(id+"F0.wireOp",EDGE,"E30.9"),sQuery(id+"F0.wireOp",EDGE,"E30.10"),sQuery(id+"F0.wireOp",EDGE,"E30.11"),sQuery(id+"F0.wireOp",EDGE,"E30.12"),sQuery(id+"F0.wireOp",EDGE,"E30.13"),sQuery(id+"F0.wireOp",EDGE,"E31.0"),sQuery(id+"F0.wireOp",EDGE,"E31.1")])],"isStart":false}),makeQuery(id+"F2.opExtrude","CAP_FACE",FACE,{"disambiguationData":[OSD([sQuery(id+"F0.wireOp",EDGE,"E1"),sQuery(id+"F0.wireOp",EDGE,"E3"),sQuery(id+"F0.wireOp",EDGE,"E5"),sQuery(id+"F0.wireOp",EDGE,"E6"),subQ15,sQuery(id+"F0.wireOp",EDGE,"E9"),sQuery(id+"F0.wireOp",EDGE,"E10"),sQuery(id+"F0.wireOp",EDGE,"E11"),subQ14,subQ13,subQ12,subQ11,subQ10,subQ9,subQ8,sQuery(id+"F0.wireOp",EDGE,"E13.MirrorCS"),sQuery(id+"F0.wireOp",EDGE,"E14.MirrorCS"),subQ7,subQ6,sQuery(id+"F0.wireOp",EDGE,"E17.MirrorCS"),sQuery(id+"F0.wireOp",EDGE,"E18.MirrorCS"),subQ5,sQuery(id+"F0.wireOp",EDGE,"E21.MirrorCS"),subQ4,subQ3,subQ2,subQ1,sQuery(id+"F0.wireOp",EDGE,"E27.MirrorCS"),sQuery(id+"F0.wireOp",EDGE,"E28.MirrorCS"),subQ0])],"isStart":false})]}),makeQuery(id+"F7.opExtrude","SWEPT_FACE",FACE,{"disambiguationData":[OSD([sQuery(id+"F6.wireOp",EDGE,"E48.top")])]}),makeQuery(id+"F7.opExtrude","SWEPT_FACE",FACE,{"disambiguationData":[OSD([sQuery(id+"F6.wireOp",EDGE,"E50.MirrorCS")])]})]});}
            var sketch = newSketch(context, id + "F14", { "sketchPlane" : qUnion([Q0])});
            skLineSegment(sketch, "E77.bottom", {"start": v(35, 3.7) * mm, "end": v(-35, 3.7) * mm});
            skLineSegment(sketch, "E77.top", {"start": v(35, -31.3) * mm, "end": v(-35, -31.3) * mm});
            skLineSegment(sketch, "E77.left", {"start": v(35, 3.7) * mm, "end": v(35, -31.3) * mm});
            skLineSegment(sketch, "E77.right", {"start": v(-35, 3.7) * mm, "end": v(-35, -31.3) * mm});
            skLineSegment(sketch, "E78.bottom", {"start": v(-24, -2.96) * mm, "end": v(23, -2.96) * mm});
            skLineSegment(sketch, "E78.top", {"start": v(-24, -17.96) * mm, "end": v(23, -17.96) * mm});
            skLineSegment(sketch, "E78.left", {"start": v(-24, -2.96) * mm, "end": v(-24, -17.96) * mm});
            skLineSegment(sketch, "E78.right", {"start": v(23, -2.96) * mm, "end": v(23, -17.96) * mm});
            skSolve(sketch);
        }
        {
            var Q0;
            Q0=makeQuery(id+"F14.imprint","IMPRINT",FACE,{"disambiguationData":[TD([[makeQuery(id+"F14.imprint","IMPRINT",EDGE,{"derivedFrom":sQuery(id+"F14.wireOp",EDGE,"E77.bottom")}),1.0]])]});
            var Q1;
            Q1=makeQuery(id+"F14.imprint","IMPRINT",FACE,{"disambiguationData":[TD([[makeQuery(id+"F14.imprint","IMPRINT",EDGE,{"derivedFrom":sQuery(id+"F14.wireOp",EDGE,"E78.bottom")}),1.0]])]});
            extrude(context, id + "F15", {"entities" : qUnion([Q0, Q1]), "depth" : 0.2 * mm, "offsetDistance" : 25 * mm});
        }
    });
